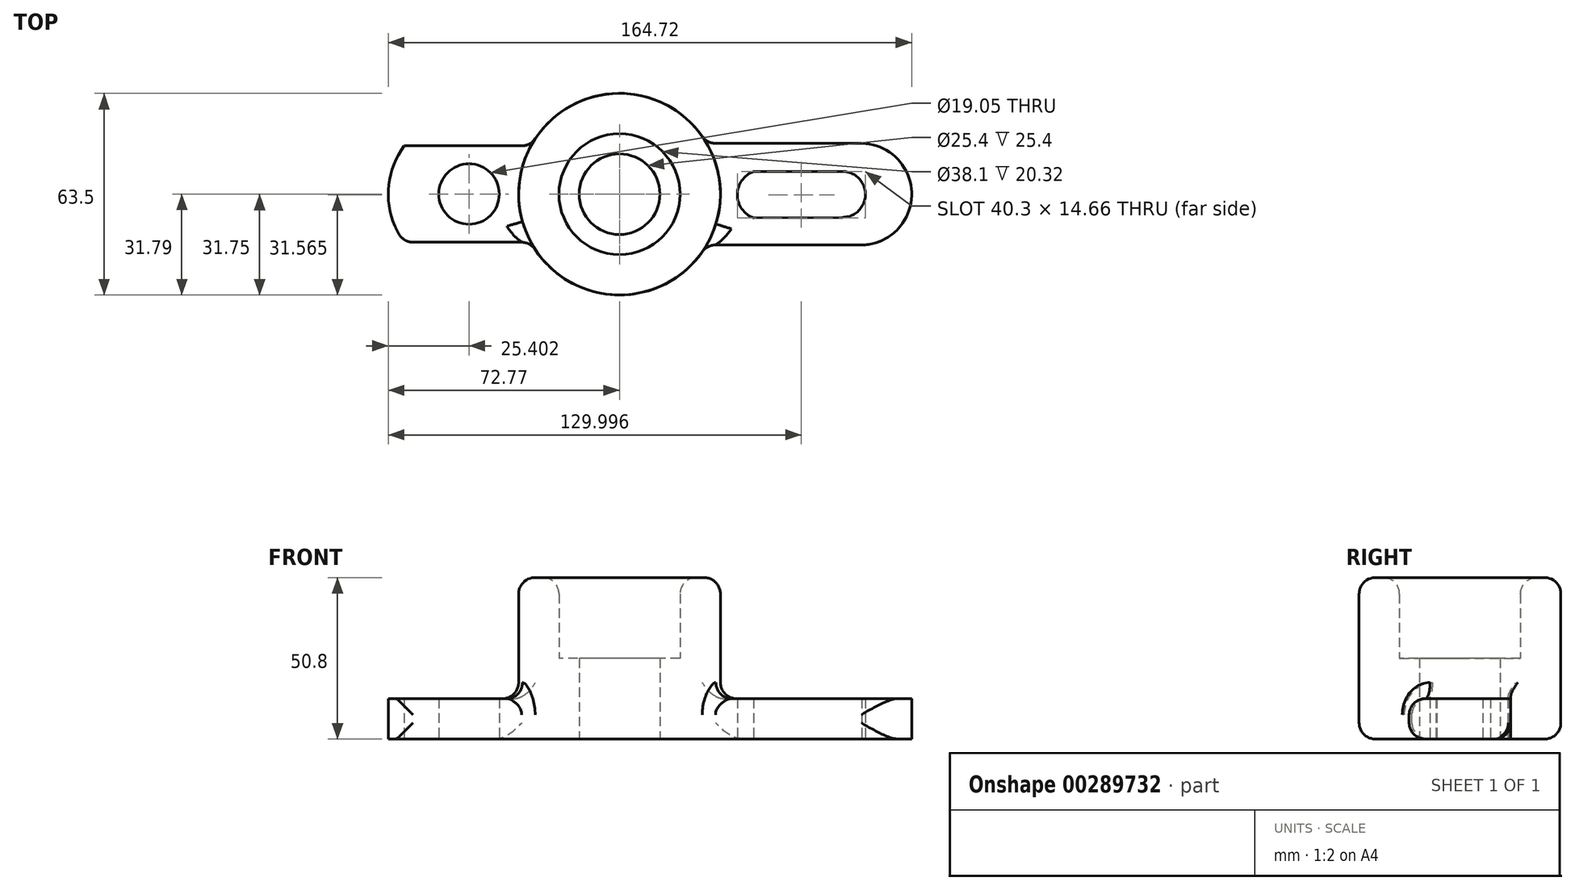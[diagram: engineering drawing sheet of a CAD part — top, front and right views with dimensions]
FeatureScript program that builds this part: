
annotation { "Feature Type Name" : "Feature", "Feature Type Description" : "" }
export const myFeature = defineFeature(function(context is Context, id is Id, definition is map)
    precondition{}
    {
        {
            var Q0;
            Q0=qCreatedBy(makeId("Top.planeOp"),FACE);
            var sketch = newSketch(context, id + "F0", { "sketchPlane" : qUnion([Q0])});
            skCircle(sketch, "E0", {"center": v(0, 0) * mm, "radius": 31.75 * mm});
            skCircle(sketch, "E1", {"center": v(0, 0) * mm, "radius": 19.05 * mm});
            skCircle(sketch, "E2", {"center": v(0, 0) * mm, "radius": 12.7 * mm});
            skLineSegment(sketch, "E3", {"start": v(27.42, 16) * mm, "end": v(76.3, 16) * mm});
            skLineSegment(sketch, "E4", {"start": v(27.42, -16) * mm, "end": v(76.32, -16) * mm});
            skArc(sketch, "E5", {"start": v(76.32, -16) * mm, "mid": v(91.95, 0.01) * mm, "end": v(76.3, 16) * mm});
            skLineSegment(sketch, "E6", {"start": v(42.21, 7.15) * mm, "end": v(70.15, 7.15) * mm});
            skArc(sketch, "E7", {"start": v(70.15, -7.3) * mm, "mid": v(77.38, -0.08) * mm, "end": v(70.15, 7.15) * mm});
            skLineSegment(sketch, "E8", {"start": v(42.21, -7.51) * mm, "end": v(70.15, -7.3) * mm});
            skArc(sketch, "E9", {"start": v(42.21, 7.15) * mm, "mid": v(37.08, -0.18) * mm, "end": v(42.21, -7.51) * mm});
            skLineSegment(sketch, "E10", {"start": v(-27.86, 15.23) * mm, "end": v(-67.73, 15.23) * mm});
            skLineSegment(sketch, "E11", {"start": v(-67.73, -15.15) * mm, "end": v(-27.9, -15.15) * mm});
            skArc(sketch, "E12", {"start": v(-67.73, 15.23) * mm, "mid": v(-72.77, 0.04) * mm, "end": v(-67.73, -15.15) * mm});
            skCircle(sketch, "E13", {"center": v(-47.37, 0.04) * mm, "radius": 9.53 * mm});
            skSolve(sketch);
        }
        {
            var Q0;
            Q0=makeQuery(id+"F0.imprint","IMPRINT",FACE,{"disambiguationData":[TD([[makeQuery(id+"F0.imprint","IMPRINT",EDGE,{"derivedFrom":sQuery(id+"F0.wireOp",EDGE,"E1")}),-1.0]])]});
            var Q1;
            {var subQ1=sQuery(id+"F0.wireOp",EDGE,"E10");Q1=makeQuery(id+"F0.imprint","IMPRINT",FACE,{"disambiguationData":[TD([[makeQuery(id+"F0.imprint","IMPRINT",EDGE,{"derivedFrom":subQ1}),1.0]])]});}
            var Q2;
            {var subQ1=sQuery(id+"F0.wireOp",EDGE,"E3");Q2=makeQuery(id+"F0.imprint","IMPRINT",FACE,{"disambiguationData":[TD([[makeQuery(id+"F0.imprint","IMPRINT",EDGE,{"derivedFrom":subQ1}),-1.0]])]});}
            extrude(context, id + "F1", {"entities" : qUnion([Q0, Q1, Q2]), "depth" : 12.7 * mm});
        }
        {
            var Q0;
            Q0=makeQuery(id+"F0.imprint","IMPRINT",FACE,{"disambiguationData":[TD([[makeQuery(id+"F0.imprint","IMPRINT",EDGE,{"derivedFrom":sQuery(id+"F0.wireOp",EDGE,"E1")}),1.0]])]});
            extrude(context, id + "F2", {"entities" : qUnion([Q0]), "operationType" : NewBodyOperationType.ADD, "depth" : 25.4 * mm});
        }
        {
            var Q0;
            Q0=makeQuery(id+"F0.imprint","IMPRINT",FACE,{"disambiguationData":[TD([[makeQuery(id+"F0.imprint","IMPRINT",EDGE,{"derivedFrom":sQuery(id+"F0.wireOp",EDGE,"E1")}),-1.0]])]});
            extrude(context, id + "F3", {"entities" : qUnion([Q0]), "operationType" : NewBodyOperationType.ADD, "depth" : 50.8 * mm});
        }
        {
            var Q0;
            Q0=makeQuery(id+"F3.opExtrude","CAP_FACE",FACE,{"disambiguationData":[OSD([sQuery(id+"F0.wireOp",EDGE,"E0"),sQuery(id+"F0.wireOp",EDGE,"E1")])],"isStart":false});
            var Q1;
            Q1=makeQuery(id+"F1.opExtrude","SWEPT_FACE",FACE,{"disambiguationData":[OSD([sQuery(id+"F0.wireOp",EDGE,"E11")])]});
            var Q2;
            {var subQ0=sQuery(id+"F0.wireOp",EDGE,"E0");Q2=makeQuery(id+"F3.boolean.opBoolean","MERGE",FACE,{"derivedFrom":[makeQuery(id+"F1.opExtrude","SWEPT_FACE",FACE,{"disambiguationData":[OSD([subQ0]),TDD([makeQuery(id+"F0.imprint","IMPRINT",EDGE,{"disambiguationData":[TD([[makeQuery(id+"F0.imprint","INTERSECT",VERTEX,{"derivedFrom":[subQ0,sQuery(id+"F0.wireOp",EDGE,"E3")]}),-1.0]])],"derivedFrom":subQ0})])]}),makeQuery(id+"F1.opExtrude","SWEPT_FACE",FACE,{"disambiguationData":[OSD([subQ0]),TDD([makeQuery(id+"F0.imprint","IMPRINT",EDGE,{"disambiguationData":[TD([[makeQuery(id+"F0.imprint","INTERSECT",VERTEX,{"derivedFrom":[subQ0,sQuery(id+"F0.wireOp",EDGE,"E4")]}),1.0]])],"derivedFrom":subQ0})])]}),makeQuery(id+"F3.opExtrude","SWEPT_FACE",FACE,{"disambiguationData":[OSD([subQ0])]})]});}
            var Q3;
            Q3=makeQuery(id+"F1.opExtrude","SWEPT_FACE",FACE,{"disambiguationData":[OSD([sQuery(id+"F0.wireOp",EDGE,"E4")])]});
            fillet(context, id + "F4", {"entities" : qUnion([Q0, Q1, Q2, Q3]), "radius" : 5.08 * mm, "tangentPropagation" : true, "allowEdgeOverflow" : false});
        }
    });
